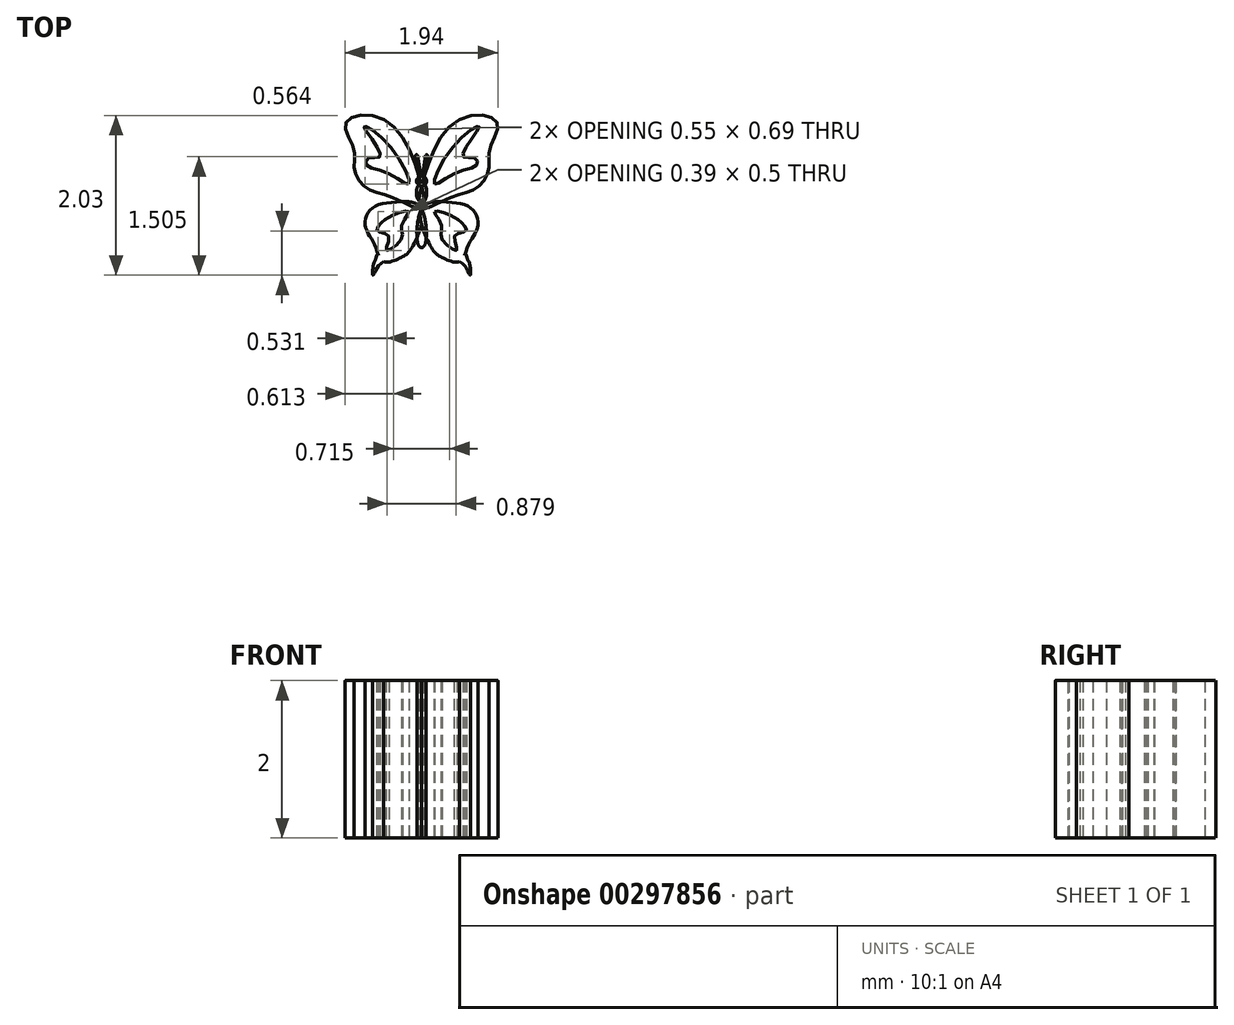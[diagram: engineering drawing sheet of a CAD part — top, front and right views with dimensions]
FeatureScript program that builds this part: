
annotation { "Feature Type Name" : "Feature", "Feature Type Description" : "" }
export const myFeature = defineFeature(function(context is Context, id is Id, definition is map)
    precondition{}
    {
        {
            var Q0;
            Q0=qCreatedBy(makeId("Top.planeOp"),FACE);
            var sketch = newSketch(context, id + "F0", { "sketchPlane" : qUnion([Q0])});
            skFitSpline(sketch, "E0", {"points": [v(0, 0) * mm, v(-0.37, 0.14) * mm, v(-0.68, 0.25) * mm, v(-0.85, 0.48) * mm, v(-0.86, 0.76) * mm, v(-0.96, 1.09) * mm, v(-0.47, 1.12) * mm, v(0, 0.28) * mm, v(0, 0) * mm]});
            skFitSpline(sketch, "E1", {"points": [v(0, 0) * mm, v(-0.36, 0.08) * mm, v(-0.63, 0) * mm, v(-0.72, -0.16) * mm, v(-0.68, -0.32) * mm, v(-0.59, -0.48) * mm, v(-0.48, -0.68) * mm, v(-0.26, -0.62) * mm, v(-0.13, -0.5) * mm, v(0, 0) * mm]});
            skFitSpline(sketch, "E2", {"points": [v(-0.54, -0.6) * mm, v(-0.58, -0.64) * mm, v(-0.6, -0.67) * mm, v(-0.62, -0.76) * mm, v(-0.62, -0.85) * mm, v(-0.48, -0.68) * mm], "startDerivative": vector(-0.35, 0.87) * mm, "endDerivative": vector(0.84, 0.45) * mm});
            skFitSpline(sketch, "E3", {"points": [v(0, 0) * mm, v(-0.06, -0.25) * mm, v(-0.06, -0.33) * mm, v(0, -0.5) * mm], "startDerivative": vector(-0.26, -0.46) * mm, "endDerivative": vector(0.47, -0.02) * mm});
            skFitSpline(sketch, "E4", {"points": [v(0, 0) * mm, v(-0.05, 0.13) * mm, v(-0.07, 0.17) * mm, v(-0.06, 0.25) * mm, v(-0.03, 0.31) * mm, v(0, 0.35) * mm], "startDerivative": vector(-0.03, 0.28) * mm, "endDerivative": vector(0.03, 0.41) * mm});
            skFitSpline(sketch, "E5", {"points": [v(-0.16, 0.3) * mm, v(-0.43, 0.45) * mm, v(-0.7, 0.56) * mm, v(-0.68, 0.64) * mm, v(-0.54, 0.65) * mm, v(-0.57, 0.8) * mm, v(-0.73, 1.04) * mm, v(-0.42, 0.8) * mm, v(-0.16, 0.3) * mm]});
            skFitSpline(sketch, "E6", {"points": [v(-0.16, -0.04) * mm, v(-0.37, -0.1) * mm, v(-0.5, -0.17) * mm, v(-0.57, -0.29) * mm, v(-0.42, -0.35) * mm, v(-0.45, -0.53) * mm, v(-0.25, -0.39) * mm, v(-0.25, -0.22) * mm, v(-0.16, -0.04) * mm]});
            skFitSpline(sketch, "E7.MirrorC", {"points": [v(0, 0) * mm, v(0.37, 0.14) * mm, v(0.68, 0.25) * mm, v(0.85, 0.48) * mm, v(0.86, 0.76) * mm, v(0.96, 1.09) * mm, v(0.47, 1.12) * mm, v(0, 0.28) * mm, v(0, 0) * mm]});
            skFitSpline(sketch, "E8.MirrorC", {"points": [v(0.16, 0.3) * mm, v(0.43, 0.45) * mm, v(0.7, 0.56) * mm, v(0.68, 0.64) * mm, v(0.54, 0.65) * mm, v(0.57, 0.8) * mm, v(0.73, 1.04) * mm, v(0.42, 0.8) * mm, v(0.16, 0.3) * mm]});
            skFitSpline(sketch, "E9.MirrorCS", {"points": [v(0, 0) * mm, v(0.05, 0.13) * mm, v(0.07, 0.17) * mm, v(0.06, 0.25) * mm, v(0.03, 0.31) * mm, v(0, 0.35) * mm], "startDerivative": vector(0.03, 0.28) * mm, "endDerivative": vector(-0.03, 0.41) * mm});
            skFitSpline(sketch, "E10.MirrorCS", {"points": [v(0, 0) * mm, v(0.06, -0.25) * mm, v(0.06, -0.33) * mm, v(0, -0.5) * mm], "startDerivative": vector(0.26, -0.46) * mm, "endDerivative": vector(-0.47, -0.02) * mm});
            skFitSpline(sketch, "E11.MirrorC", {"points": [v(0, 0) * mm, v(0.36, 0.08) * mm, v(0.63, 0) * mm, v(0.72, -0.16) * mm, v(0.68, -0.32) * mm, v(0.59, -0.48) * mm, v(0.48, -0.68) * mm, v(0.26, -0.62) * mm, v(0.13, -0.5) * mm, v(0, 0) * mm]});
            skFitSpline(sketch, "E12.MirrorC", {"points": [v(0.16, -0.04) * mm, v(0.37, -0.1) * mm, v(0.5, -0.17) * mm, v(0.57, -0.29) * mm, v(0.42, -0.35) * mm, v(0.45, -0.53) * mm, v(0.25, -0.39) * mm, v(0.25, -0.22) * mm, v(0.16, -0.04) * mm]});
            skFitSpline(sketch, "E13.MirrorCS", {"points": [v(0.54, -0.6) * mm, v(0.58, -0.64) * mm, v(0.6, -0.67) * mm, v(0.62, -0.76) * mm, v(0.62, -0.85) * mm, v(0.48, -0.68) * mm], "startDerivative": vector(0.35, 0.87) * mm, "endDerivative": vector(-0.84, 0.45) * mm});
            skFitSpline(sketch, "E14", {"points": [v(0, 0.35) * mm, v(-0.07, 0.68) * mm, v(-0.05, 0.68) * mm], "startDerivative": vector(-0.17, 0.58) * mm, "endDerivative": vector(0.13, -0.04) * mm});
            skPoint(sketch, "E15.end.orphan", {"position": v(0.05, 0.68) * mm});
            skFitSpline(sketch, "E16.MirrorCS", {"points": [v(0, 0.35) * mm, v(0.07, 0.68) * mm, v(0.05, 0.68) * mm], "startDerivative": vector(0.17, 0.58) * mm, "endDerivative": vector(-0.13, -0.04) * mm});
            skLineSegment(sketch, "E17", {"start": v(-0.05, 0.68) * mm, "end": v(0, 0.35) * mm});
            skLineSegment(sketch, "E18", {"start": v(0.05, 0.68) * mm, "end": v(0, 0.35) * mm});
            skCircle(sketch, "E19", {"center": v(0, 0.35) * mm, "radius": 0.06 * mm});
            skSolve(sketch);
        }
        {
            var Q0;
            Q0=makeQuery(id+"F0.imprint","IMPRINT",FACE,{"disambiguationData":[TD([[makeQuery(id+"F0.imprint","IMPRINT",EDGE,{"derivedFrom":sQuery(id+"F0.wireOp",EDGE,"E5")}),1.0]])]});
            var Q1;
            Q1=makeQuery(id+"F0.imprint","IMPRINT",FACE,{"disambiguationData":[TD([[makeQuery(id+"F0.imprint","IMPRINT",EDGE,{"derivedFrom":sQuery(id+"F0.wireOp",EDGE,"E8.MirrorC")}),-1.0]])]});
            var Q2;
            Q2=makeQuery(id+"F0.imprint","IMPRINT",FACE,{"disambiguationData":[TD([[makeQuery(id+"F0.imprint","IMPRINT",EDGE,{"derivedFrom":sQuery(id+"F0.wireOp",EDGE,"E12.MirrorC")}),1.0]])]});
            var Q3;
            Q3=makeQuery(id+"F0.imprint","IMPRINT",FACE,{"disambiguationData":[TD([[makeQuery(id+"F0.imprint","IMPRINT",EDGE,{"derivedFrom":sQuery(id+"F0.wireOp",EDGE,"E6")}),-1.0]])]});
            var Q4;
            {var subQ0=sQuery(id+"F0.wireOp",EDGE,"E2");Q4=makeQuery(id+"F0.imprint","IMPRINT",FACE,{"disambiguationData":[TD([[makeQuery(id+"F0.imprint","IMPRINT",EDGE,{"derivedFrom":subQ0}),1.0]])]});}
            var Q5;
            {var subQ0=sQuery(id+"F0.wireOp",EDGE,"E13.MirrorCS");Q5=makeQuery(id+"F0.imprint","IMPRINT",FACE,{"disambiguationData":[TD([[makeQuery(id+"F0.imprint","IMPRINT",EDGE,{"derivedFrom":subQ0}),-1.0]])]});}
            var Q6;
            {var subQ0=sQuery(id+"F0.wireOp",EDGE,"E3");var subQ1=sQuery(id+"F0.wireOp",EDGE,"E1");var subQ2=makeQuery(id+"F0.imprint","INTERSECT",VERTEX,{"derivedFrom":[subQ1,subQ0]});Q6=makeQuery(id+"F0.imprint","IMPRINT",FACE,{"disambiguationData":[TD([[makeQuery(id+"F0.imprint","IMPRINT",EDGE,{"disambiguationData":[TD([[subQ2,-1.0]])],"derivedFrom":subQ1}),-1.0]])]});}
            var Q7;
            {var subQ0=sQuery(id+"F0.wireOp",EDGE,"E11.MirrorC");var subQ1=sQuery(id+"F0.wireOp",EDGE,"E1");var subQ3=makeQuery(id+"F0.imprint","INTERSECT",VERTEX,{"derivedFrom":[subQ1,subQ0]});Q7=makeQuery(id+"F0.imprint","IMPRINT",FACE,{"disambiguationData":[TD([[makeQuery(id+"F0.imprint","IMPRINT",EDGE,{"disambiguationData":[TD([[subQ3,-1.0]])],"derivedFrom":subQ1}),1.0]])]});}
            var Q8;
            {var subQ0=sQuery(id+"F0.wireOp",EDGE,"E7.MirrorC");var subQ1=sQuery(id+"F0.wireOp",EDGE,"E0");var subQ2=makeQuery(id+"F0.imprint","INTERSECT",VERTEX,{"derivedFrom":[subQ1,subQ0]});Q8=makeQuery(id+"F0.imprint","IMPRINT",FACE,{"disambiguationData":[TD([[makeQuery(id+"F0.imprint","IMPRINT",EDGE,{"disambiguationData":[TD([[subQ2,-1.0]])],"derivedFrom":subQ1}),-1.0]])]});}
            var Q9;
            {var subQ0=sQuery(id+"F0.wireOp",EDGE,"E17");var subQ1=sQuery(id+"F0.wireOp",EDGE,"E14");var subQ2=makeQuery(id+"F0.imprint","INTERSECT",VERTEX,{"derivedFrom":[subQ1,subQ0]});Q9=makeQuery(id+"F0.imprint","IMPRINT",FACE,{"disambiguationData":[TD([[makeQuery(id+"F0.imprint","IMPRINT",EDGE,{"disambiguationData":[TD([[subQ2,1.0]])],"derivedFrom":subQ1}),-1.0]])]});}
            var Q10;
            {var subQ0=sQuery(id+"F0.wireOp",EDGE,"E18");var subQ1=sQuery(id+"F0.wireOp",EDGE,"E16.MirrorCS");var subQ2=makeQuery(id+"F0.imprint","INTERSECT",VERTEX,{"derivedFrom":[subQ1,subQ0]});Q10=makeQuery(id+"F0.imprint","IMPRINT",FACE,{"disambiguationData":[TD([[makeQuery(id+"F0.imprint","IMPRINT",EDGE,{"disambiguationData":[TD([[subQ2,1.0]])],"derivedFrom":subQ1}),1.0]])]});}
            var Q11;
            {var subQ5=sQuery(id+"F0.wireOp",EDGE,"E4");var subQ7=sQuery(id+"F0.wireOp",EDGE,"E0");var subQ8=makeQuery(id+"F0.imprint","INTERSECT",VERTEX,{"derivedFrom":[subQ7,subQ5]});Q11=makeQuery(id+"F0.imprint","IMPRINT",FACE,{"disambiguationData":[TD([[makeQuery(id+"F0.imprint","IMPRINT",EDGE,{"disambiguationData":[TD([[subQ8,-1.0]])],"derivedFrom":subQ7}),1.0]])]});}
            var Q12;
            {var subQ0=sQuery(id+"F0.wireOp",EDGE,"E9.MirrorCS");var subQ1=sQuery(id+"F0.wireOp",EDGE,"E7.MirrorC");var subQ2=makeQuery(id+"F0.imprint","INTERSECT",VERTEX,{"derivedFrom":[subQ1,subQ0]});Q12=makeQuery(id+"F0.imprint","IMPRINT",FACE,{"disambiguationData":[TD([[makeQuery(id+"F0.imprint","IMPRINT",EDGE,{"disambiguationData":[TD([[subQ2,-1.0]])],"derivedFrom":subQ1}),1.0]])]});}
            var Q13;
            {var subQ0=sQuery(id+"F0.wireOp",EDGE,"E4");var subQ1=sQuery(id+"F0.wireOp",EDGE,"E0");var subQ2=makeQuery(id+"F0.imprint","INTERSECT",VERTEX,{"derivedFrom":[subQ1,subQ0]});Q13=makeQuery(id+"F0.imprint","IMPRINT",FACE,{"disambiguationData":[TD([[makeQuery(id+"F0.imprint","IMPRINT",EDGE,{"disambiguationData":[TD([[subQ2,-1.0]])],"derivedFrom":subQ1}),-1.0]])]});}
            var Q14;
            {var subQ0=sQuery(id+"F0.wireOp",EDGE,"E19");var subQ1=sQuery(id+"F0.wireOp",EDGE,"E7.MirrorC");var subQ2=makeQuery(id+"F0.imprint","INTERSECT",VERTEX,{"disambiguationData":[OD(0.0)],"derivedFrom":[subQ1,subQ0]});Q14=makeQuery(id+"F0.imprint","IMPRINT",FACE,{"disambiguationData":[TD([[makeQuery(id+"F0.imprint","IMPRINT",EDGE,{"disambiguationData":[TD([[subQ2,-1.0]])],"derivedFrom":subQ1}),-1.0]])]});}
            var Q15;
            {var subQ1=sQuery(id+"F0.wireOp",EDGE,"E14");var subQ3=sQuery(id+"F0.wireOp",EDGE,"E19");var subQ4=makeQuery(id+"F0.imprint","INTERSECT",VERTEX,{"derivedFrom":[subQ1,subQ3]});Q15=makeQuery(id+"F0.imprint","IMPRINT",FACE,{"disambiguationData":[TD([[makeQuery(id+"F0.imprint","IMPRINT",EDGE,{"disambiguationData":[TD([[subQ4,1.0]])],"derivedFrom":subQ3}),1.0]])]});}
            var Q16;
            {var subQ1=sQuery(id+"F0.wireOp",EDGE,"E17");var subQ3=sQuery(id+"F0.wireOp",EDGE,"E19");var subQ4=makeQuery(id+"F0.imprint","INTERSECT",VERTEX,{"derivedFrom":[subQ1,subQ3]});Q16=makeQuery(id+"F0.imprint","IMPRINT",FACE,{"disambiguationData":[TD([[makeQuery(id+"F0.imprint","IMPRINT",EDGE,{"disambiguationData":[TD([[subQ4,1.0]])],"derivedFrom":subQ3}),1.0]])]});}
            var Q17;
            {var subQ1=sQuery(id+"F0.wireOp",EDGE,"E16.MirrorCS");var subQ3=sQuery(id+"F0.wireOp",EDGE,"E19");var subQ4=makeQuery(id+"F0.imprint","INTERSECT",VERTEX,{"derivedFrom":[subQ1,subQ3]});Q17=makeQuery(id+"F0.imprint","IMPRINT",FACE,{"disambiguationData":[TD([[makeQuery(id+"F0.imprint","IMPRINT",EDGE,{"disambiguationData":[TD([[subQ4,-1.0]])],"derivedFrom":subQ3}),1.0]])]});}
            var Q18;
            {var subQ0=sQuery(id+"F0.wireOp",EDGE,"E19");var subQ1=sQuery(id+"F0.wireOp",EDGE,"E0");var subQ2=makeQuery(id+"F0.imprint","INTERSECT",VERTEX,{"disambiguationData":[OD(0.0)],"derivedFrom":[subQ1,subQ0]});Q18=makeQuery(id+"F0.imprint","IMPRINT",FACE,{"disambiguationData":[TD([[makeQuery(id+"F0.imprint","IMPRINT",EDGE,{"disambiguationData":[TD([[subQ2,-1.0]])],"derivedFrom":subQ1}),1.0]])]});}
            var Q19;
            {var subQ0=sQuery(id+"F0.wireOp",EDGE,"E7.MirrorC");var subQ2=sQuery(id+"F0.wireOp",EDGE,"E1");var subQ4=makeQuery(id+"F0.imprint","INTERSECT",VERTEX,{"derivedFrom":[subQ2,subQ0]});Q19=makeQuery(id+"F0.imprint","IMPRINT",FACE,{"disambiguationData":[TD([[makeQuery(id+"F0.imprint","IMPRINT",EDGE,{"disambiguationData":[TD([[subQ4,1.0]])],"derivedFrom":subQ0}),1.0]])]});}
            var Q20;
            {var subQ0=sQuery(id+"F0.wireOp",EDGE,"E7.MirrorC");var subQ1=sQuery(id+"F0.wireOp",EDGE,"E1");var subQ3=makeQuery(id+"F0.imprint","INTERSECT",VERTEX,{"derivedFrom":[subQ1,subQ0]});Q20=makeQuery(id+"F0.imprint","IMPRINT",FACE,{"disambiguationData":[TD([[makeQuery(id+"F0.imprint","IMPRINT",EDGE,{"disambiguationData":[TD([[subQ3,1.0]])],"derivedFrom":subQ1}),1.0]])]});}
            var Q21;
            {var subQ0=sQuery(id+"F0.wireOp",EDGE,"E11.MirrorC");var subQ1=sQuery(id+"F0.wireOp",EDGE,"E0");var subQ3=makeQuery(id+"F0.imprint","INTERSECT",VERTEX,{"derivedFrom":[subQ1,subQ0]});Q21=makeQuery(id+"F0.imprint","IMPRINT",FACE,{"disambiguationData":[TD([[makeQuery(id+"F0.imprint","IMPRINT",EDGE,{"disambiguationData":[TD([[subQ3,-1.0]])],"derivedFrom":subQ1}),-1.0]])]});}
            var Q22;
            {var subQ0=sQuery(id+"F0.wireOp",EDGE,"E9.MirrorCS");var subQ1=sQuery(id+"F0.wireOp",EDGE,"E0");var subQ2=makeQuery(id+"F0.imprint","INTERSECT",VERTEX,{"derivedFrom":[subQ1,subQ0]});Q22=makeQuery(id+"F0.imprint","IMPRINT",FACE,{"disambiguationData":[TD([[makeQuery(id+"F0.imprint","IMPRINT",EDGE,{"disambiguationData":[TD([[subQ2,-1.0]])],"derivedFrom":subQ1}),-1.0]])]});}
            extrude(context, id + "F1", {"entities" : qUnion([Q0, Q1, Q2, Q3, Q4, Q5, Q6, Q7, Q8, Q9, Q10, Q11, Q12, Q13, Q14, Q15, Q16, Q17, Q18, Q19, Q20, Q21, Q22]), "depth" : 2 * mm});
        }
    });
